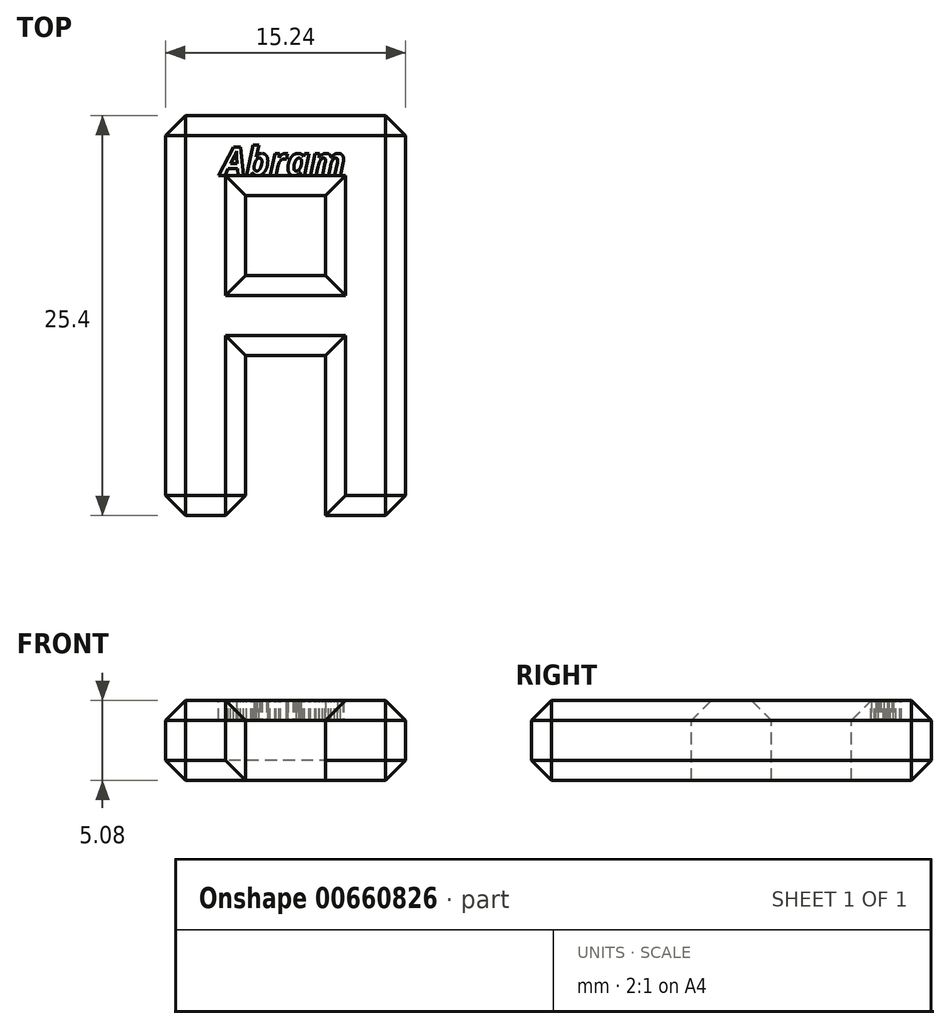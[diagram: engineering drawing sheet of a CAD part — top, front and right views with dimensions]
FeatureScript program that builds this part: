
annotation { "Feature Type Name" : "Feature", "Feature Type Description" : "" }
export const myFeature = defineFeature(function(context is Context, id is Id, definition is map)
    precondition{}
    {
        {
            var Q0;
            Q0=qCreatedBy(makeId("Top.planeOp"),FACE);
            var sketch = newSketch(context, id + "F0", { "sketchPlane" : qUnion([Q0])});
            skLineSegment(sketch, "E0.bottom", {"start": v(7.62, 12.7) * mm, "end": v(-7.62, 12.7) * mm});
            skLineSegment(sketch, "E0.top", {"start": v(7.62, -12.7) * mm, "end": v(-7.62, -12.7) * mm});
            skLineSegment(sketch, "E0.left", {"start": v(7.62, 12.7) * mm, "end": v(7.62, -12.7) * mm});
            skLineSegment(sketch, "E0.right", {"start": v(-7.62, 12.7) * mm, "end": v(-7.62, -12.7) * mm});
            skPoint(sketch, "E0.middle", {"position": v(0, 0) * mm});
            skSolve(sketch);
        }
        {
            var Q0;
            Q0=makeQuery(id+"F0.imprint","IMPRINT",FACE,{"disambiguationData":[TD([[makeQuery(id+"F0.imprint","IMPRINT",EDGE,{"derivedFrom":sQuery(id+"F0.wireOp",EDGE,"E0.bottom")}),1.0]])]});
            extrude(context, id + "F1", {"entities" : qUnion([Q0]), "depth" : 5.08 * mm, "offsetDistance" : 25.4 * mm});
        }
        {
            var Q0;
            Q0=makeQuery(id+"F1.opExtrude","CAP_FACE",FACE,{"disambiguationData":[OSD([sQuery(id+"F0.wireOp",EDGE,"E0.bottom"),sQuery(id+"F0.wireOp",EDGE,"E0.top"),sQuery(id+"F0.wireOp",EDGE,"E0.left"),sQuery(id+"F0.wireOp",EDGE,"E0.right")])],"isStart":false});
            var sketch = newSketch(context, id + "F2", { "sketchPlane" : qUnion([Q0])});
            skLineSegment(sketch, "E1.bottom", {"start": v(-2.54, -12.7) * mm, "end": v(2.54, -12.7) * mm});
            skLineSegment(sketch, "E1.top", {"start": v(-2.54, -2.54) * mm, "end": v(2.54, -2.54) * mm});
            skLineSegment(sketch, "E1.left", {"start": v(-2.54, -12.7) * mm, "end": v(-2.54, -2.54) * mm});
            skLineSegment(sketch, "E1.right", {"start": v(2.54, -12.7) * mm, "end": v(2.54, -2.54) * mm});
            skLineSegment(sketch, "E2.bottom", {"start": v(-2.54, 7.62) * mm, "end": v(2.54, 7.62) * mm});
            skLineSegment(sketch, "E2.top", {"start": v(-2.54, 2.54) * mm, "end": v(2.54, 2.54) * mm});
            skLineSegment(sketch, "E2.left", {"start": v(-2.54, 7.62) * mm, "end": v(-2.54, 2.54) * mm});
            skLineSegment(sketch, "E2.right", {"start": v(2.54, 7.62) * mm, "end": v(2.54, 2.54) * mm});
            skSolve(sketch);
        }
        {
            var Q0;
            Q0=makeQuery(id+"F2.imprint","IMPRINT",FACE,{"disambiguationData":[TD([[makeQuery(id+"F2.imprint","IMPRINT",EDGE,{"derivedFrom":sQuery(id+"F2.wireOp",EDGE,"E2.bottom")}),-1.0]])]});
            var Q1;
            Q1=makeQuery(id+"F2.imprint","IMPRINT",FACE,{"disambiguationData":[TD([[makeQuery(id+"F2.imprint","IMPRINT",EDGE,{"derivedFrom":sQuery(id+"F2.wireOp",EDGE,"E1.bottom")}),-1.0]])]});
            extrude(context, id + "F3", {"entities" : qUnion([Q0, Q1]), "operationType" : NewBodyOperationType.REMOVE, "oppositeDirection" : true, "depth" : 5.08 * mm, "offsetDistance" : 25.4 * mm});
        }
        {
            var Q0;
            Q0=makeQuery(id+"F3.boolean.opBoolean","COPY",EDGE,{"derivedFrom":makeQuery(id+"F3.opExtrude","CAP_EDGE",EDGE,{"disambiguationData":[OSD([sQuery(id+"F2.wireOp",EDGE,"E2.left")])],"isStart":true})});
            var Q1;
            Q1=makeQuery(id+"F3.boolean.opBoolean","COPY",EDGE,{"derivedFrom":makeQuery(id+"F3.opExtrude","CAP_EDGE",EDGE,{"disambiguationData":[OSD([sQuery(id+"F2.wireOp",EDGE,"E2.bottom")])],"isStart":true})});
            var Q2;
            Q2=makeQuery(id+"F3.boolean.opBoolean","COPY",EDGE,{"derivedFrom":makeQuery(id+"F3.opExtrude","CAP_EDGE",EDGE,{"disambiguationData":[OSD([sQuery(id+"F2.wireOp",EDGE,"E2.right")])],"isStart":true})});
            var Q3;
            Q3=makeQuery(id+"F3.boolean.opBoolean","COPY",EDGE,{"derivedFrom":makeQuery(id+"F3.opExtrude","CAP_EDGE",EDGE,{"disambiguationData":[OSD([sQuery(id+"F2.wireOp",EDGE,"E2.top")])],"isStart":true})});
            var Q4;
            Q4=makeQuery(id+"F3.boolean.opBoolean","COPY",EDGE,{"derivedFrom":makeQuery(id+"F3.opExtrude","CAP_EDGE",EDGE,{"disambiguationData":[OSD([sQuery(id+"F2.wireOp",EDGE,"E1.top")])],"isStart":true})});
            var Q5;
            Q5=makeQuery(id+"F3.boolean.opBoolean","COPY",EDGE,{"derivedFrom":makeQuery(id+"F3.opExtrude","CAP_EDGE",EDGE,{"disambiguationData":[OSD([sQuery(id+"F2.wireOp",EDGE,"E1.left")])],"isStart":true})});
            var Q6;
            Q6=makeQuery(id+"F1.opExtrude","CAP_FACE",FACE,{"disambiguationData":[OSD([sQuery(id+"F0.wireOp",EDGE,"E0.bottom"),sQuery(id+"F0.wireOp",EDGE,"E0.top"),sQuery(id+"F0.wireOp",EDGE,"E0.left"),sQuery(id+"F0.wireOp",EDGE,"E0.right")])],"isStart":false});
            var Q7;
            Q7=makeQuery(id+"F3.boolean.opBoolean","COPY",EDGE,{"derivedFrom":makeQuery(id+"F3.opExtrude","SWEPT_EDGE",EDGE,{"disambiguationData":[OSD([sQuery(id+"F0.wireOp",EDGE,"E0.top"),sQuery(id+"F2.wireOp",EDGE,"E1.bottom"),sQuery(id+"F2.wireOp",EDGE,"E1.left")])]})});
            var Q8;
            Q8=makeQuery(id+"F1.opExtrude","SWEPT_EDGE",EDGE,{"disambiguationData":[OSD([sQuery(id+"F0.wireOp",EDGE,"E0.top"),sQuery(id+"F0.wireOp",EDGE,"E0.right")])]});
            var Q9;
            Q9=makeQuery(id+"F3.boolean.opBoolean","COPY",EDGE,{"derivedFrom":makeQuery(id+"F3.opExtrude","SWEPT_EDGE",EDGE,{"disambiguationData":[OSD([sQuery(id+"F0.wireOp",EDGE,"E0.top"),sQuery(id+"F2.wireOp",EDGE,"E1.bottom"),sQuery(id+"F2.wireOp",EDGE,"E1.right")])]})});
            var Q10;
            Q10=makeQuery(id+"F1.opExtrude","SWEPT_EDGE",EDGE,{"disambiguationData":[OSD([sQuery(id+"F0.wireOp",EDGE,"E0.top"),sQuery(id+"F0.wireOp",EDGE,"E0.left")])]});
            var Q11;
            Q11=makeQuery(id+"F1.opExtrude","SWEPT_EDGE",EDGE,{"disambiguationData":[OSD([sQuery(id+"F0.wireOp",EDGE,"E0.bottom"),sQuery(id+"F0.wireOp",EDGE,"E0.left")])]});
            var Q12;
            Q12=makeQuery(id+"F1.opExtrude","SWEPT_EDGE",EDGE,{"disambiguationData":[OSD([sQuery(id+"F0.wireOp",EDGE,"E0.bottom"),sQuery(id+"F0.wireOp",EDGE,"E0.right")])]});
            var Q13;
            Q13=makeQuery(id+"F1.opExtrude","CAP_EDGE",EDGE,{"disambiguationData":[OSD([sQuery(id+"F0.wireOp",EDGE,"E0.bottom")])],"isStart":true});
            var Q14;
            Q14=makeQuery(id+"F3.boolean.opBoolean","COPY",EDGE,{"derivedFrom":makeQuery(id+"F3.opExtrude","CAP_EDGE",EDGE,{"disambiguationData":[OSD([sQuery(id+"F2.wireOp",EDGE,"E2.left")])],"isStart":false})});
            var Q15;
            Q15=makeQuery(id+"F3.boolean.opBoolean","COPY",EDGE,{"derivedFrom":makeQuery(id+"F3.opExtrude","CAP_EDGE",EDGE,{"disambiguationData":[OSD([sQuery(id+"F2.wireOp",EDGE,"E2.right")])],"isStart":false})});
            var Q16;
            Q16=makeQuery(id+"F3.boolean.opBoolean","COPY",EDGE,{"derivedFrom":makeQuery(id+"F3.opExtrude","CAP_EDGE",EDGE,{"disambiguationData":[OSD([sQuery(id+"F2.wireOp",EDGE,"E2.bottom")])],"isStart":false})});
            var Q17;
            Q17=makeQuery(id+"F3.boolean.opBoolean","COPY",EDGE,{"derivedFrom":makeQuery(id+"F3.opExtrude","CAP_EDGE",EDGE,{"disambiguationData":[OSD([sQuery(id+"F2.wireOp",EDGE,"E2.top")])],"isStart":false})});
            var Q18;
            Q18=makeQuery(id+"F3.boolean.opBoolean","COPY",EDGE,{"derivedFrom":makeQuery(id+"F3.opExtrude","CAP_EDGE",EDGE,{"disambiguationData":[OSD([sQuery(id+"F2.wireOp",EDGE,"E1.top")])],"isStart":false})});
            var Q19;
            Q19=makeQuery(id+"F3.boolean.opBoolean","COPY",EDGE,{"derivedFrom":makeQuery(id+"F3.opExtrude","CAP_EDGE",EDGE,{"disambiguationData":[OSD([sQuery(id+"F2.wireOp",EDGE,"E1.left")])],"isStart":false})});
            var Q20;
            Q20=makeQuery(id+"F3.boolean.opBoolean","COPY",EDGE,{"derivedFrom":makeQuery(id+"F3.opExtrude","CAP_EDGE",EDGE,{"disambiguationData":[OSD([sQuery(id+"F2.wireOp",EDGE,"E1.right")])],"isStart":false})});
            var Q21;
            Q21=makeQuery(id+"F1.opExtrude","CAP_EDGE",EDGE,{"disambiguationData":[OSD([sQuery(id+"F0.wireOp",EDGE,"E0.right")])],"isStart":true});
            var Q22;
            Q22=makeQuery(id+"F1.opExtrude","CAP_EDGE",EDGE,{"disambiguationData":[OSD([sQuery(id+"F0.wireOp",EDGE,"E0.left")])],"isStart":true});
            var Q23;
            {var subQ0=sQuery(id+"F0.wireOp",EDGE,"E0.right");var subQ1=sQuery(id+"F0.wireOp",EDGE,"E0.top");Q23=makeQuery(id+"F3.boolean.opBoolean","SPLIT",EDGE,{"disambiguationData":[TD([makeQuery(id+"F1.opExtrude","SWEPT_FACE",FACE,{"disambiguationData":[OSD([subQ0])]})])],"derivedFrom":makeQuery(id+"F1.opExtrude","CAP_EDGE",EDGE,{"disambiguationData":[OSD([subQ1])],"isStart":true})});}
            var Q24;
            {var subQ0=sQuery(id+"F0.wireOp",EDGE,"E0.left");var subQ1=sQuery(id+"F0.wireOp",EDGE,"E0.top");Q24=makeQuery(id+"F3.boolean.opBoolean","SPLIT",EDGE,{"disambiguationData":[TD([makeQuery(id+"F1.opExtrude","SWEPT_FACE",FACE,{"disambiguationData":[OSD([subQ0])]})])],"derivedFrom":makeQuery(id+"F1.opExtrude","CAP_EDGE",EDGE,{"disambiguationData":[OSD([subQ1])],"isStart":true})});}
            chamfer(context, id + "F4", {"entities" : qUnion([Q0, Q1, Q2, Q3, Q4, Q5, Q6, Q7, Q8, Q9, Q10, Q11, Q12, Q13, Q14, Q15, Q16, Q17, Q18, Q19, Q20, Q21, Q22, Q23, Q24]), "width" : 1.27 * mm, "tangentPropagation" : true});
        }
        {
            var Q0;
            Q0=makeQuery(id+"F1.opExtrude","CAP_FACE",FACE,{"disambiguationData":[OSD([sQuery(id+"F0.wireOp",EDGE,"E0.bottom"),sQuery(id+"F0.wireOp",EDGE,"E0.top"),sQuery(id+"F0.wireOp",EDGE,"E0.left"),sQuery(id+"F0.wireOp",EDGE,"E0.right")])],"isStart":false});
            var sketch = newSketch(context, id + "F5", { "sketchPlane" : qUnion([Q0])});
            skText(sketch, "E3", { "text": "Abram", "fontName": "OpenSans-BoldItalic.ttf"});
            const initialGuessF5  = {"E3": [-0.00409, 0.0089, 1, 0, 0.00181]};
            skSetInitialGuess(sketch, initialGuessF5);
            skSolve(sketch);
        }
        {
            var Q0;
            Q0 = qSketchRegion(id + "F5", true);
            extrude(context, id + "F6", {"entities" : qUnion([Q0]), "operationType" : NewBodyOperationType.REMOVE, "oppositeDirection" : true, "depth" : 1.27 * mm, "offsetDistance" : 25.4 * mm});
        }
    });
